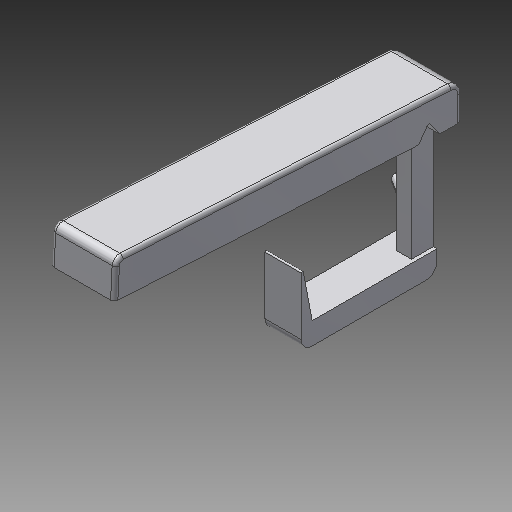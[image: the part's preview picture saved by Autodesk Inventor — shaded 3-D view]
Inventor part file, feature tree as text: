
AUTODESK INVENTOR PART (.ipt)
format: ipt  version: 2018 (Build 220112000, 112)  size: 299,008 bytes
history: native  units: mm
features: extrude x7, fillet x6, other x3, draft x1, chamfer x1
ambient origin geometry x8: Origin, YZ Plane, XZ Plane, XY Plane, X Axis, Y Axis, Z Axis, Center Point
bodies: Solid1 (feature_tree)
feature tree (18):
  other  "Key Sketch"
  extrude  "Upper Key"  Depth=10.0mm
  extrude  "Lower Key"  Depth=1.0mm
  other  "Hinge Cut Sketch"
  extrude  "Hinge Cut"  Depth=10.0mm TaperAngle=0.0deg
  extrude  "Hinge Cut 2"  Depth=3.0mm
  other  "Lever Sketch"
  extrude  "Vertical Lever"  Depth=3.0mm
  extrude  "Horizontal Lever"  Depth=33.6625mm
  extrude  "Spring Hook"  Depth=0.5mm
  draft  "FaceDraft3"
  chamfer  "Chamfer1"  Distance=3.0mm
  fillet  "Fillet9"  Radius=6.0mm
  fillet  "Fillet10"  Radius=4.0mm
  fillet  "Fillet5"  Radius=10.0mm
  fillet  "Fillet4"  [1 undecoded]
  fillet  "Fillet11"  Radius=3.0mm
  fillet  "Fillet14"  Radius=2.3mm
note: 1 required parameter value undecoded (feature->parameter linkage not recoverable at this tier; creation-order binding heuristic only, values carry confidence <= 0.55)
